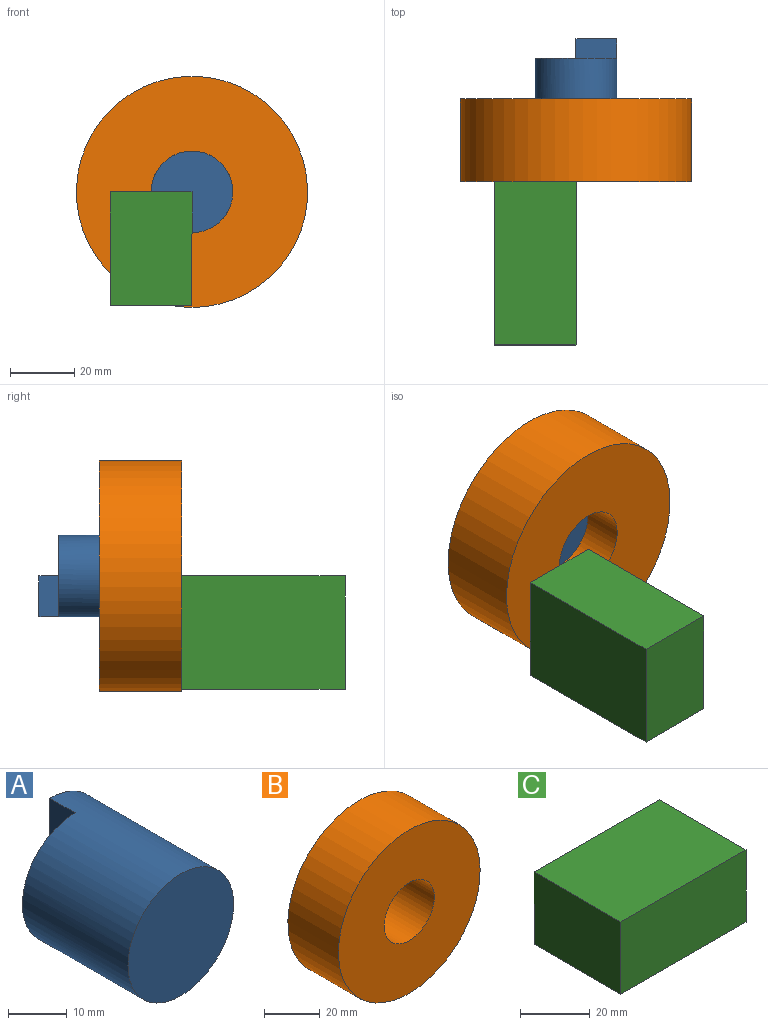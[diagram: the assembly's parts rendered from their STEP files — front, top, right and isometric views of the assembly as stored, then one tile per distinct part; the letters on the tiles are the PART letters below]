
ASSEMBLY  parts=3 mates=2
PART A: 6 faces, bbox 25.4x31.5x25.4 mm
  f0: cylinder r=12.7mm len=31.52mm, axis (0,1,0), area 2148.9mm2, adj f1,f2,f3,f4,f5
  f1: plane 25.4x25.4mm, normal (0,-1,0), area 506.7mm2, adj f0
  f2: plane 25.4x25.4mm, normal (0,1,0), area 380mm2, adj f0,f3,f4
  f3: plane 12.7x6.12mm, normal (0,0,-1), area 77.7mm2, adj f0,f2,f4,f5
  f4: plane 12.7x6.12mm, normal (-1,0,0), area 77.7mm2, adj f0,f2,f3,f5
  f5: plane 12.7x12.7mm, normal (0,1,0), area 126.7mm2, adj f0,f3,f4
PART B: 4 faces, bbox 71.8x25.7x71.8 mm
  f0: cylinder r=12.7mm len=25.65mm, axis (0,1,0), area 2047.1mm2, adj f2,f3
  f1: cylinder r=35.92mm len=71.85mm, axis (0,1,0), area 5790.7mm2, adj f2,f3
  f2: plane 71.85x71.85mm, normal (0,-1,0), area 3547.8mm2, adj f0,f1
  f3: plane 71.85x71.85mm, normal (0,1,0), area 3547.8mm2, adj f0,f1
PART C: 6 faces, bbox 50.8x35.3x25.4 mm
  f0: plane 50.8x35.31mm, normal (0,0,1), area 1793.5mm2, adj f1,f3,f4,f5
  f1: plane 35.31x25.4mm, normal (-1,0,0), area 896.8mm2, adj f0,f2,f4,f5
  f2: plane 50.8x35.31mm, normal (0,0,-1), area 1793.5mm2, adj f1,f3,f4,f5
  f3: plane 35.31x25.4mm, normal (1,0,0), area 896.8mm2, adj f0,f2,f4,f5
  f4: plane 50.8x25.4mm, normal (0,-1,0), area 1290.3mm2, adj f0,f1,f2,f3
  f5: plane 50.8x25.4mm, normal (0,1,0), area 1290.3mm2, adj f0,f1,f2,f3
PLACE A rot(axis=(0,1,0),90deg) t=(8.1,60.87,40.88)mm
PLACE B rot(axis=(0.08,0.97,0.21),0deg) t=(8.1,48.29,40.88)mm
PLACE C rot(axis=(0.58,0.58,0.58),120deg) t=(11.5,-1.71,40.88)mm
MATE revolute A.f0 <-> B.f0  axis (0,-1,0) through (8.1,35.47,40.88)mm
MATE revolute C.f3 <-> B.f0  axis (0,1,0) through (8.1,22.64,40.88)mm
